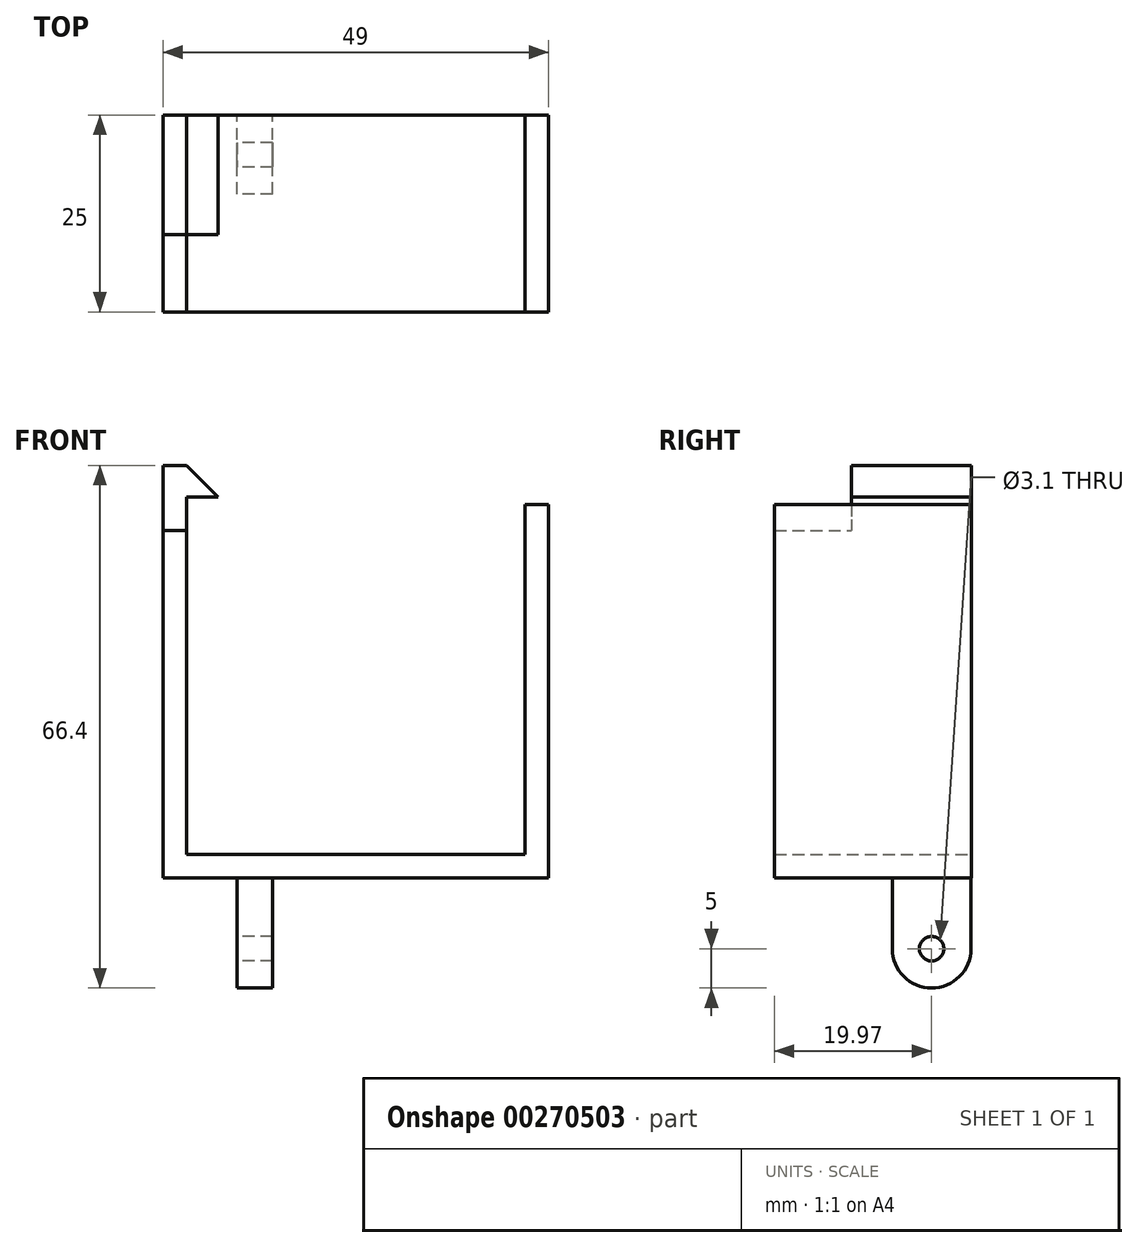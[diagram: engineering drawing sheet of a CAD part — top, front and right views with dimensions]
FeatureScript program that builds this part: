
annotation { "Feature Type Name" : "Feature", "Feature Type Description" : "" }
export const myFeature = defineFeature(function(context is Context, id is Id, definition is map)
    precondition{}
    {
        {
            var Q0;
            Q0=qCreatedBy(makeId("Front.planeOp"),FACE);
            var sketch = newSketch(context, id + "F0", { "sketchPlane" : qUnion([Q0])});
            skLineSegment(sketch, "E0.bottom", {"start": v(0, 0) * mm, "end": v(43, 0) * mm});
            skLineSegment(sketch, "E0.top", {"start": v(0, 3) * mm, "end": v(43, 3) * mm});
            skLineSegment(sketch, "E0.left", {"start": v(0, 0) * mm, "end": v(0, 3) * mm});
            skLineSegment(sketch, "E0.right", {"start": v(43, 0) * mm, "end": v(43, 3) * mm});
            skLineSegment(sketch, "E1.bottom", {"start": v(43, 0) * mm, "end": v(46, 0) * mm});
            skLineSegment(sketch, "E1.top", {"start": v(43, 47.4) * mm, "end": v(46, 47.4) * mm});
            skLineSegment(sketch, "E1.left", {"start": v(43, 0) * mm, "end": v(43, 47.4) * mm});
            skLineSegment(sketch, "E1.right", {"start": v(46, 0) * mm, "end": v(46, 47.4) * mm});
            skLineSegment(sketch, "E2.bottom", {"start": v(0, 0) * mm, "end": v(-3, 0) * mm});
            skLineSegment(sketch, "E2.top", {"start": v(0, 52.4) * mm, "end": v(-3, 52.4) * mm});
            skLineSegment(sketch, "E2.left", {"start": v(0, 0) * mm, "end": v(0, 52.4) * mm});
            skLineSegment(sketch, "E2.right", {"start": v(-3, 0) * mm, "end": v(-3, 52.4) * mm});
            skLineSegment(sketch, "E3", {"start": v(0, 52.4) * mm, "end": v(4, 48.4) * mm});
            skLineSegment(sketch, "E4", {"start": v(0, 48.4) * mm, "end": v(4, 48.4) * mm});
            skLineSegment(sketch, "E5", {"start": v(0, 48.4) * mm, "end": v(0, 52.4) * mm});
            skSolve(sketch);
        }
        {
            var Q0;
            Q0=makeQuery(id+"F0.imprint","IMPRINT",FACE,{"disambiguationData":[TD([[makeQuery(id+"F0.imprint","IMPRINT",EDGE,{"derivedFrom":sQuery(id+"F0.wireOp",EDGE,"E3")}),-1.0]])]});
            var Q1;
            Q1=makeQuery(id+"F0.imprint","IMPRINT",FACE,{"disambiguationData":[TD([[makeQuery(id+"F0.imprint","IMPRINT",EDGE,{"derivedFrom":sQuery(id+"F0.wireOp",EDGE,"E2.bottom")}),-1.0]])]});
            var Q2;
            {var subQ0=sQuery(id+"F0.wireOp",EDGE,"E0.bottom");Q2=makeQuery(id+"F0.imprint","IMPRINT",FACE,{"disambiguationData":[TD([[makeQuery(id+"F0.imprint","IMPRINT",EDGE,{"derivedFrom":subQ0}),1.0]])]});}
            var Q3;
            {var subQ3=sQuery(id+"F0.wireOp",EDGE,"E1.bottom");Q3=makeQuery(id+"F0.imprint","IMPRINT",FACE,{"disambiguationData":[TD([[makeQuery(id+"F0.imprint","IMPRINT",EDGE,{"derivedFrom":subQ3}),1.0]])]});}
            extrude(context, id + "F1", {"entities" : qUnion([Q0, Q1, Q2, Q3]), "depth" : 25 * mm});
        }
        {
            var Q0;
            Q0=makeQuery(id+"F1.opExtrude","SWEPT_FACE",FACE,{"disambiguationData":[OSD([sQuery(id+"F0.wireOp",EDGE,"E0.bottom"),sQuery(id+"F0.wireOp",EDGE,"E1.bottom"),sQuery(id+"F0.wireOp",EDGE,"E2.bottom")])]});
            var sketch = newSketch(context, id + "F2", { "sketchPlane" : qUnion([Q0])});
            skLineSegment(sketch, "E6", {"start": v(-3, 0) * mm, "end": v(8.68, 0) * mm, "construction": true});
            skLineSegment(sketch, "E7", {"start": v(8.68, 0) * mm, "end": v(8.68, 25) * mm, "construction": true});
            skLineSegment(sketch, "E8", {"start": v(8.68, 0) * mm, "end": v(8.68, 5.03) * mm, "construction": true});
            skLineSegment(sketch, "E9.bottom", {"start": v(10.93, 10.03) * mm, "end": v(6.43, 10.03) * mm});
            skLineSegment(sketch, "E9.top", {"start": v(10.93, 0.03) * mm, "end": v(6.43, 0.03) * mm});
            skLineSegment(sketch, "E9.left", {"start": v(10.93, 10.03) * mm, "end": v(10.93, 0.03) * mm});
            skLineSegment(sketch, "E9.right", {"start": v(6.43, 10.03) * mm, "end": v(6.43, 0.03) * mm});
            skPoint(sketch, "E9.middle", {"position": v(8.68, 5.03) * mm});
            skSolve(sketch);
        }
        {
            var Q0;
            Q0=makeQuery(id+"F2.imprint","IMPRINT",FACE,{"disambiguationData":[TD([[makeQuery(id+"F2.imprint","IMPRINT",EDGE,{"derivedFrom":sQuery(id+"F2.wireOp",EDGE,"E9.bottom")}),1.0]])]});
            extrude(context, id + "F3", {"entities" : qUnion([Q0]), "operationType" : NewBodyOperationType.ADD, "depth" : 14 * mm});
        }
        {
            var Q0;
            Q0=makeQuery(id+"F3.opExtrude","CAP_EDGE",EDGE,{"disambiguationData":[OSD([sQuery(id+"F2.wireOp",EDGE,"E9.bottom")])],"isStart":false});
            var Q1;
            Q1=makeQuery(id+"F3.opExtrude","CAP_EDGE",EDGE,{"disambiguationData":[OSD([sQuery(id+"F2.wireOp",EDGE,"E9.top")])],"isStart":false});
            fillet(context, id + "F4", {"entities" : qUnion([Q0, Q1]), "radius" : 5 * mm, "tangentPropagation" : true, "allowEdgeOverflow" : false});
        }
        {
            var Q0;
            Q0=makeQuery(id+"F3.opExtrude","SWEPT_FACE",FACE,{"disambiguationData":[OSD([sQuery(id+"F2.wireOp",EDGE,"E9.right")])]});
            var sketch = newSketch(context, id + "F5", { "sketchPlane" : qUnion([Q0])});
            skCircle(sketch, "E10", {"center": v(5.03, -9) * mm, "radius": 1.55 * mm});
            skLineSegment(sketch, "E11", {"start": v(5.03, 0) * mm, "end": v(5.03, -7.45) * mm});
            skSolve(sketch);
        }
        {
            var Q0;
            Q0=makeQuery(id+"F5.imprint","IMPRINT",FACE,{"disambiguationData":[TD([[makeQuery(id+"F5.imprint","IMPRINT",EDGE,{"derivedFrom":sQuery(id+"F5.wireOp",EDGE,"E10")}),1.0]])]});
            extrude(context, id + "F6", {"entities" : qUnion([Q0]), "operationType" : NewBodyOperationType.REMOVE, "oppositeDirection" : true, "depth" : 5 * mm});
        }
        {
            var Q0;
            Q0=makeQuery(id+"F1.opExtrude","SWEPT_FACE",FACE,{"disambiguationData":[OSD([sQuery(id+"F0.wireOp",EDGE,"E2.right")])]});
            var sketch = newSketch(context, id + "F7", { "sketchPlane" : qUnion([Q0])});
            skLineSegment(sketch, "E12.bottom", {"start": v(25, 52.4) * mm, "end": v(15.19, 52.4) * mm});
            skLineSegment(sketch, "E12.top", {"start": v(25, 44.14) * mm, "end": v(15.19, 44.14) * mm});
            skLineSegment(sketch, "E12.left", {"start": v(25, 52.4) * mm, "end": v(25, 44.14) * mm});
            skLineSegment(sketch, "E12.right", {"start": v(15.19, 52.4) * mm, "end": v(15.19, 44.14) * mm});
            skSolve(sketch);
        }
        {
            var Q0;
            Q0=makeQuery(id+"F7.imprint","IMPRINT",FACE,{"disambiguationData":[TD([[makeQuery(id+"F7.imprint","IMPRINT",EDGE,{"derivedFrom":sQuery(id+"F7.wireOp",EDGE,"E12.bottom")}),1.0]])]});
            extrude(context, id + "F8", {"entities" : qUnion([Q0]), "operationType" : NewBodyOperationType.REMOVE, "oppositeDirection" : true, "depth" : 7 * mm, "offsetDistance" : 25 * mm});
        }
    });
